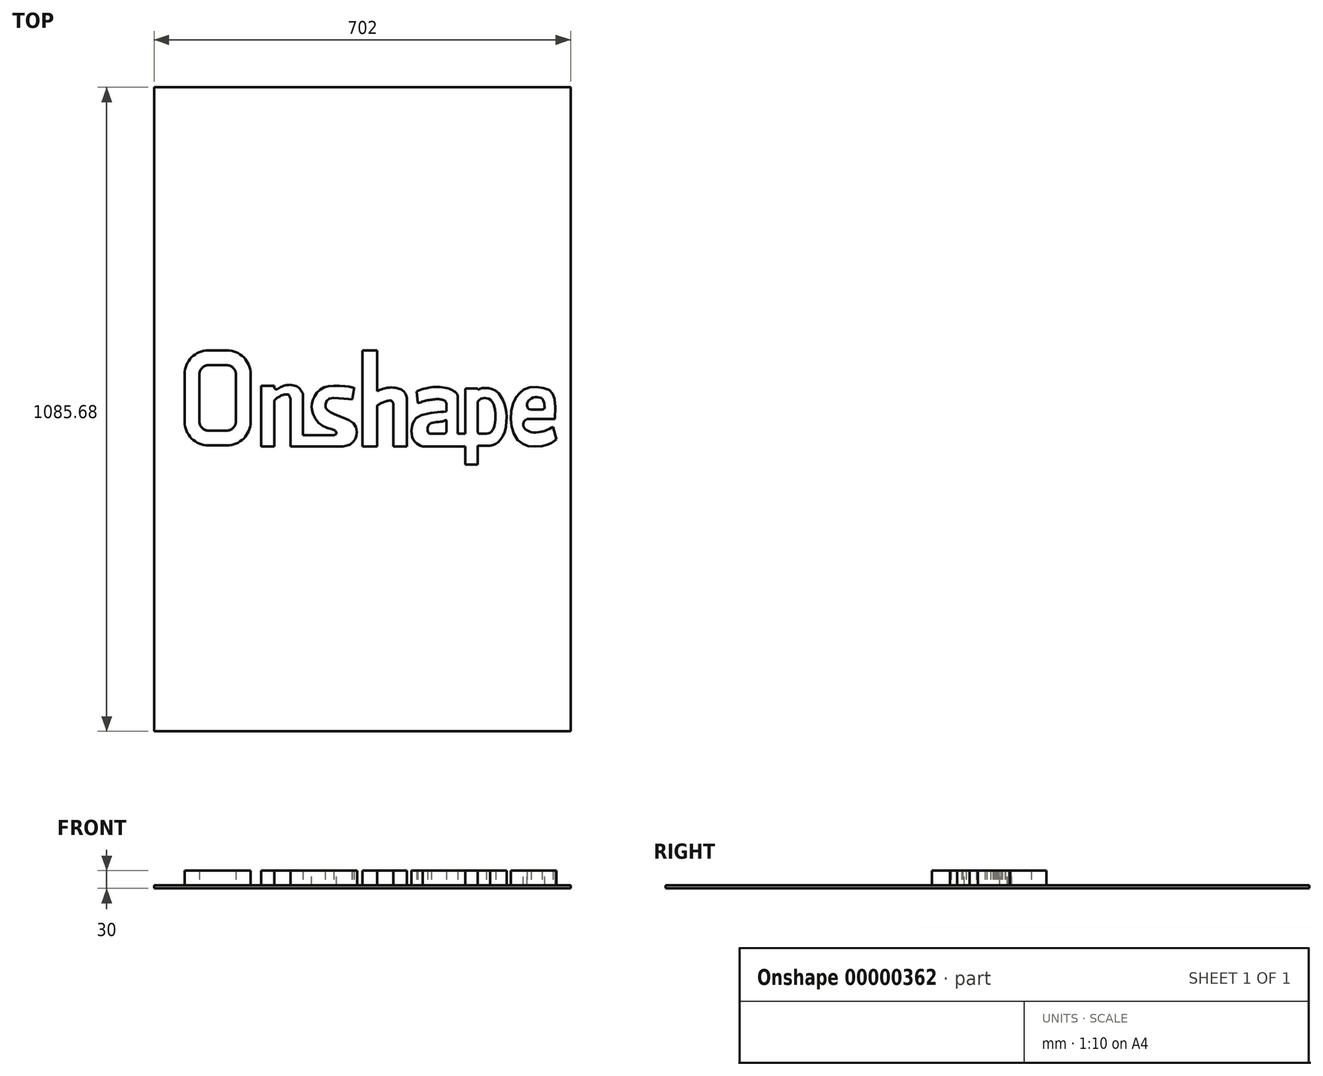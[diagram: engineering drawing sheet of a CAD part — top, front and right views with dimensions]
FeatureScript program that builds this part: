
annotation { "Feature Type Name" : "Feature", "Feature Type Description" : "" }
export const myFeature = defineFeature(function(context is Context, id is Id, definition is map)
    precondition{}
    {
        {
            var Q0;
            Q0 = qCreatedBy(makeId("Top.planeOp"), FACE);
            var sketch = newSketch(context, id + "F0", { "sketchPlane" : qUnion([Q0])});
            skLineSegment(sketch, "E0.bottom", {"start": v(-351, 542.84) * mm, "end": v(351, 542.84) * mm});
            skLineSegment(sketch, "E0.top", {"start": v(-351, -542.84) * mm, "end": v(351, -542.84) * mm});
            skLineSegment(sketch, "E0.left", {"start": v(-351, 542.84) * mm, "end": v(-351, -542.84) * mm});
            skLineSegment(sketch, "E0.right", {"start": v(351, 542.84) * mm, "end": v(351, -542.84) * mm});
            skLineSegment(sketch, "E1", {"start": v(0, 0) * mm, "end": v(285.59, 0) * mm, "construction": true});
            skLineSegment(sketch, "E2", {"start": v(0, 0) * mm, "end": v(0, 273.23) * mm, "construction": true});
            skPoint(sketch, "E3", {"position": v(351, 0) * mm});
            skPoint(sketch, "E4", {"position": v(0, 542.84) * mm});
            skSolve(sketch);
        }
        {
            var Q0;
            Q0=makeQuery(id+"F0.imprint","IMPRINT",FACE,{"disambiguationData":[TD([[makeQuery(id+"F0.imprint","IMPRINT",EDGE,{"derivedFrom":sQuery(id+"F0.wireOp",EDGE,"E0.bottom")}),-1.0]])]});
            extrude(context, id + "F1", {"entities" : qUnion([Q0]), "depth" : 5 * mm});
        }
        {
            var Q0;
            Q0=makeQuery(id+"F1.opExtrude","CAP_FACE",FACE,{"disambiguationData":[OSD([sQuery(id+"F0.wireOp",EDGE,"E0.bottom"),sQuery(id+"F0.wireOp",EDGE,"E0.top"),sQuery(id+"F0.wireOp",EDGE,"E0.left"),sQuery(id+"F0.wireOp",EDGE,"E0.right")])],"isStart":false});
            var sketch = newSketch(context, id + "F2", { "sketchPlane" : qUnion([Q0])});
            skLineSegment(sketch, "E5", {"start": v(-299.7, 59.23) * mm, "end": v(-299.7, -20.92) * mm});
            skLineSegment(sketch, "E6", {"start": v(-259.7, -60.92) * mm, "end": v(-228.47, -60.92) * mm});
            skLineSegment(sketch, "E7", {"start": v(-188.47, -20.92) * mm, "end": v(-188.47, 59.23) * mm});
            skLineSegment(sketch, "E8", {"start": v(-228.47, 99.23) * mm, "end": v(-259.7, 99.23) * mm});
            skPoint(sketch, "E9.visualSharp", {"position": v(-299.7, -60.92) * mm});
            skArc(sketch, "E9.filletArc", {"start": v(-299.7, -20.92) * mm, "mid": v(-287.98, -49.2) * mm, "end": v(-259.7, -60.92) * mm});
            skPoint(sketch, "E10.visualSharp", {"position": v(-188.47, -60.92) * mm});
            skArc(sketch, "E10.filletArc", {"start": v(-228.47, -60.92) * mm, "mid": v(-200.19, -49.2) * mm, "end": v(-188.47, -20.92) * mm});
            skPoint(sketch, "E11.visualSharp", {"position": v(-299.7, 99.23) * mm});
            skArc(sketch, "E11.filletArc", {"start": v(-259.7, 99.23) * mm, "mid": v(-287.98, 87.51) * mm, "end": v(-299.7, 59.23) * mm});
            skPoint(sketch, "E12.visualSharp", {"position": v(-188.47, 99.23) * mm});
            skArc(sketch, "E12.filletArc", {"start": v(-188.47, 59.23) * mm, "mid": v(-200.19, 87.51) * mm, "end": v(-228.47, 99.23) * mm});
            skArc(sketch, "E13.0", {"start": v(-259.7, 74.23) * mm, "mid": v(-270.3, 69.83) * mm, "end": v(-274.7, 59.23) * mm});
            skLineSegment(sketch, "E13.1", {"start": v(-228.47, 74.23) * mm, "end": v(-259.7, 74.23) * mm});
            skArc(sketch, "E13.2", {"start": v(-213.47, 59.23) * mm, "mid": v(-217.87, 69.83) * mm, "end": v(-228.47, 74.23) * mm});
            skLineSegment(sketch, "E13.3", {"start": v(-213.47, -20.92) * mm, "end": v(-213.47, 59.23) * mm});
            skArc(sketch, "E13.4", {"start": v(-228.47, -35.92) * mm, "mid": v(-217.87, -31.52) * mm, "end": v(-213.47, -20.92) * mm});
            skLineSegment(sketch, "E13.5", {"start": v(-274.7, 59.23) * mm, "end": v(-274.7, -20.92) * mm});
            skLineSegment(sketch, "E13.6", {"start": v(-259.7, -35.92) * mm, "end": v(-228.47, -35.92) * mm});
            skArc(sketch, "E13.7", {"start": v(-274.7, -20.92) * mm, "mid": v(-270.3, -31.52) * mm, "end": v(-259.7, -35.92) * mm});
            skLineSegment(sketch, "E14", {"start": v(-170.45, -62.44) * mm, "end": v(-170.45, 39.68) * mm});
            skLineSegment(sketch, "E15", {"start": v(-170.45, 39.68) * mm, "end": v(-148.72, 39.68) * mm});
            skLineSegment(sketch, "E16", {"start": v(-148.72, 39.68) * mm, "end": v(-148.72, 37.04) * mm});
            skLineSegment(sketch, "E17", {"start": v(-148.72, -62.44) * mm, "end": v(-170.45, -62.44) * mm});
            skLineSegment(sketch, "E18", {"start": v(-121.4, 17.58) * mm, "end": v(-121.4, -62.44) * mm});
            skLineSegment(sketch, "E19", {"start": v(-121.4, -62.44) * mm, "end": v(-48.13, -62.44) * mm});
            skLineSegment(sketch, "E20", {"start": v(-48.13, -43.6) * mm, "end": v(-100.29, -43.6) * mm});
            skLineSegment(sketch, "E21", {"start": v(-100.29, -43.6) * mm, "end": v(-100.29, 25.35) * mm});
            skFitSpline(sketch, "E22", {"points": [v(-148.72, 14.77) * mm, v(-138.78, 22.22) * mm, v(-125.75, 24.7) * mm, v(-121.4, 18.5) * mm], "startDerivative": vector(24.47, 22.54) * mm, "endDerivative": vector(10.61, -28.3) * mm});
            skFitSpline(sketch, "E23", {"points": [v(-148.72, 36.08) * mm, v(-146.57, 33.73) * mm, v(-143.96, 33.73) * mm, v(-137.44, 37.38) * mm, v(-127.78, 40.78) * mm, v(-114.46, 40) * mm, v(-106.37, 35.3) * mm, v(-100.29, 26.76) * mm], "startDerivative": vector(21.71, -30.96) * mm, "endDerivative": vector(33.67, -55.34) * mm});
            skLineSegment(sketch, "E24.trimOffspring", {"start": v(-148.72, 12.57) * mm, "end": v(-148.72, -62.44) * mm});
            skFitSpline(sketch, "E25", {"points": [v(-48.13, -43.6) * mm, v(-44.9, -42.6) * mm, v(-43.7, -40.64) * mm, v(-45.58, -36.09) * mm, v(-57.63, -32.04) * mm, v(-75.73, -20.85) * mm, v(-84.33, -3.82) * mm, v(-85.46, 5.7) * mm, v(-84.17, 13.46) * mm, v(-78.2, 26.16) * mm, v(-66.3, 36) * mm, v(-48.13, 39.37) * mm, v(-25.89, 38.59) * mm, v(-17.86, 37.03) * mm], "startDerivative": vector(84.75, 14.56) * mm, "endDerivative": vector(103.74, -25.5) * mm});
            skLineSegment(sketch, "E26", {"start": v(-48.13, -62.44) * mm, "end": v(-32.73, -62.44) * mm});
            skFitSpline(sketch, "E27", {"points": [v(-32.73, -62.44) * mm, v(-21.15, -59.62) * mm, v(-12.78, -51.3) * mm, v(-9.11, -40.31) * mm, v(-14.98, -23.83) * mm, v(-38.05, -12.1) * mm, v(-54.17, -4.42) * mm, v(-61.86, 2.18) * mm, v(-61.5, 11.7) * mm, v(-54.17, 18.3) * mm, v(-32.73, 17.93) * mm, v(-17.17, 16.46) * mm], "startDerivative": vector(97.21, 0) * mm, "endDerivative": vector(103.18, -17.03) * mm});
            skLineSegment(sketch, "E28", {"start": v(-17.17, 16.46) * mm, "end": v(-13.93, 36.16) * mm});
            skLineSegment(sketch, "E29", {"start": v(-13.93, 36.16) * mm, "end": v(-17.86, 37.03) * mm});
            skLineSegment(sketch, "E30", {"start": v(-0.12, -62.44) * mm, "end": v(-0.12, 99.47) * mm});
            skLineSegment(sketch, "E31", {"start": v(-0.12, 99.47) * mm, "end": v(24.62, 99.47) * mm});
            skLineSegment(sketch, "E32", {"start": v(24.62, 99.47) * mm, "end": v(24.62, 30.35) * mm});
            skLineSegment(sketch, "E33", {"start": v(24.62, -62.44) * mm, "end": v(-0.12, -62.44) * mm});
            skLineSegment(sketch, "E34", {"start": v(52.3, -62.44) * mm, "end": v(52.3, 9.6) * mm});
            skLineSegment(sketch, "E35", {"start": v(74.9, 12.38) * mm, "end": v(74.9, -62.44) * mm});
            skLineSegment(sketch, "E36", {"start": v(74.9, -62.44) * mm, "end": v(52.3, -62.44) * mm});
            skFitSpline(sketch, "E37", {"points": [v(24.62, 5.44) * mm, v(27.86, 8.13) * mm, v(34.95, 11.8) * mm, v(43.26, 14.24) * mm, v(49.13, 14) * mm, v(51.82, 10.75) * mm, v(52.3, 8.38) * mm], "startDerivative": vector(19.33, 17.96) * mm, "endDerivative": vector(0, -32.88) * mm});
            skFitSpline(sketch, "E38", {"points": [v(24.62, 30.35) * mm, v(29.1, 32.6) * mm, v(36.01, 34.84) * mm, v(42.58, 36.4) * mm, v(53.13, 36.4) * mm, v(62.46, 34.5) * mm, v(70.24, 29.66) * mm, v(74.22, 22.05) * mm, v(74.9, 15.3) * mm, v(74.9, 12.38) * mm], "startDerivative": vector(44.62, 25.05) * mm, "endDerivative": vector(-0.44, -37.07) * mm});
            skLineSegment(sketch, "E39.trimOffspring", {"start": v(24.62, 5.44) * mm, "end": v(24.62, -62.44) * mm});
            skFitSpline(sketch, "E40", {"points": [v(91.47, 29.81) * mm, v(100.87, 33.76) * mm, v(109.8, 36) * mm, v(121.47, 37.76) * mm, v(137.6, 36.75) * mm, v(148.95, 33.38) * mm, v(156.51, 28.8) * mm, v(160.7, 22.33) * mm], "startDerivative": vector(46.04, 27.08) * mm, "endDerivative": vector(2.85, -63.73) * mm});
            skLineSegment(sketch, "E41", {"start": v(160.7, 22.33) * mm, "end": v(160.7, -41.26) * mm});
            skLineSegment(sketch, "E42", {"start": v(101.8, -62.44) * mm, "end": v(173.45, -62.44) * mm});
            skFitSpline(sketch, "E43", {"points": [v(101.8, -62.44) * mm, v(94.97, -60.1) * mm, v(89.25, -55.3) * mm, v(84.04, -47.25) * mm, v(82.98, -33.71) * mm, v(84.45, -25.96) * mm, v(89.86, -15.84) * mm, v(100.35, -9.98) * mm, v(114.96, -6.23) * mm, v(130.08, -4.58) * mm, v(141.68, -3.82) * mm], "startDerivative": vector(-83.06, 22.5) * mm, "endDerivative": vector(90.2, 15.78) * mm});
            skLineSegment(sketch, "E44", {"start": v(141.68, -3.82) * mm, "end": v(141.68, 9.14) * mm});
            skLineSegment(sketch, "E45", {"start": v(91.47, 29.81) * mm, "end": v(93.14, 10.22) * mm});
            skFitSpline(sketch, "E46", {"points": [v(93.14, 10.22) * mm, v(102.54, 13.17) * mm, v(110.48, 15.2) * mm, v(119.18, 16.47) * mm, v(126.74, 17.06) * mm, v(133.29, 16.56) * mm, v(138.37, 14.63) * mm, v(141.68, 9.14) * mm], "startDerivative": vector(58.12, 18.51) * mm, "endDerivative": vector(-2.77, -59.3) * mm});
            skLineSegment(sketch, "E47", {"start": v(141.68, -18.9) * mm, "end": v(141.68, -36.46) * mm});
            skLineSegment(sketch, "E48", {"start": v(116.36, -41.46) * mm, "end": v(136.68, -41.46) * mm});
            skFitSpline(sketch, "E49", {"points": [v(116.36, -41.46) * mm, v(112.4, -40.43) * mm, v(110.68, -38.46) * mm, v(109.69, -34.27) * mm, v(110.68, -28.76) * mm, v(114.38, -24.32) * mm, v(123.1, -21.93) * mm, v(132.88, -20.86) * mm, v(136.9, -19.71) * mm, v(139.17, -18.9) * mm, v(140.44, -18.15) * mm, v(141.3, -18.44) * mm, v(141.68, -18.9) * mm], "startDerivative": vector(-49.56, 8.3) * mm, "endDerivative": vector(5.14, -15.4) * mm});
            skLineSegment(sketch, "E50", {"start": v(160.7, -41.26) * mm, "end": v(173.45, -41.26) * mm});
            skLineSegment(sketch, "E51", {"start": v(173.45, -41.26) * mm, "end": v(173.45, 33.12) * mm});
            skLineSegment(sketch, "E52", {"start": v(173.45, -62.44) * mm, "end": v(173.45, -93.45) * mm});
            skLineSegment(sketch, "E53", {"start": v(173.45, -93.45) * mm, "end": v(194.65, -93.45) * mm});
            skLineSegment(sketch, "E54", {"start": v(194.65, -93.45) * mm, "end": v(194.65, -61.56) * mm});
            skLineSegment(sketch, "E55", {"start": v(194.65, -61.56) * mm, "end": v(215.6, -61.56) * mm});
            skLineSegment(sketch, "E56", {"start": v(194.65, -38.26) * mm, "end": v(194.65, 12.53) * mm});
            skLineSegment(sketch, "E57", {"start": v(175.45, 35.12) * mm, "end": v(194.65, 35.12) * mm});
            skLineSegment(sketch, "E58", {"start": v(197.65, -41.26) * mm, "end": v(209.14, -41.26) * mm});
            skFitSpline(sketch, "E59", {"points": [v(194.65, 12.53) * mm, v(197.22, 15.65) * mm, v(199.78, 17.28) * mm, v(203.26, 18.68) * mm, v(208.38, 18.9) * mm, v(214.66, 16.82) * mm, v(220.24, 10.54) * mm, v(224.2, -3.65) * mm, v(224.2, -18.53) * mm, v(222.34, -29.23) * mm, v(217.92, -37.6) * mm, v(213.5, -40.4) * mm, v(209.14, -41.26) * mm], "startDerivative": vector(39.46, 54.88) * mm, "endDerivative": vector(-66.44, -9.1) * mm});
            skFitSpline(sketch, "E60", {"points": [v(194.65, 35.12) * mm, v(194.65, 34.24) * mm, v(195.2, 33.45) * mm, v(197.3, 33.82) * mm, v(200.08, 35.12) * mm, v(204.76, 35.8) * mm, v(215.73, 35.12) * mm, v(226.27, 30.15) * mm, v(232.85, 22.81) * mm, v(239.05, 10.48) * mm, v(242.37, -1.64) * mm, v(243.18, -18.11) * mm, v(240.18, -36.82) * mm, v(233.54, -50.2) * mm, v(226.74, -57.3) * mm, v(221.64, -59.78) * mm, v(215.6, -61.56) * mm], "startDerivative": vector(-4.32, -40.56) * mm, "endDerivative": vector(-113.2, -25.5) * mm});
            skPoint(sketch, "E61.orphan", {"position": v(160.7, 22.88) * mm});
            skFitSpline(sketch, "E62", {"points": [v(326.96, -50.83) * mm, v(320.02, -56.08) * mm, v(315.24, -58.6) * mm, v(309.1, -60.81) * mm, v(299.72, -62.54) * mm, v(285.17, -62.73) * mm, v(276.37, -60.93) * mm, v(268.48, -56.75) * mm, v(259.32, -48.7) * mm, v(253.39, -35.65) * mm, v(250.61, -20.8) * mm, v(250.93, -3.85) * mm, v(254.2, 10.02) * mm, v(259.94, 21.4) * mm, v(265.37, 27.44) * mm, v(270.42, 32.05) * mm, v(278.77, 36) * mm, v(290.84, 37.54) * mm, v(303.57, 36.22) * mm, v(313.45, 33.15) * mm, v(318.72, 29.2) * mm, v(322.67, 21.95) * mm, v(324.64, 13.83) * mm, v(324.86, -16.25) * mm], "startDerivative": vector(-94.33, -93.91) * mm, "endDerivative": vector(-10.07, -512.06) * mm});
            skLineSegment(sketch, "E63", {"start": v(324.86, -16.25) * mm, "end": v(277.89, -16.25) * mm});
            skFitSpline(sketch, "E64", {"points": [v(277.89, -16.25) * mm, v(273.27, -19.98) * mm, v(271.31, -24.74) * mm, v(271.72, -28.5) * mm, v(273.39, -32) * mm, v(276.36, -34.76) * mm, v(281.36, -37.5) * mm, v(290.54, -39.2) * mm, v(302.45, -37.83) * mm, v(308.36, -35.97) * mm, v(315.28, -32.97) * mm, v(321.28, -29.83) * mm], "startDerivative": vector(-38.92, -19.1) * mm, "endDerivative": vector(57.68, 31.07) * mm});
            skLineSegment(sketch, "E65", {"start": v(321.28, -29.83) * mm, "end": v(326.96, -50.83) * mm});
            skLineSegment(sketch, "E66", {"start": v(284.38, -0.68) * mm, "end": v(303.3, -0.68) * mm});
            skFitSpline(sketch, "E67", {"points": [v(303.3, -0.68) * mm, v(305.2, -0.1) * mm, v(306.86, 1.74) * mm, v(307.15, 5.36) * mm, v(306.8, 10.1) * mm, v(304.71, 15.56) * mm, v(301.1, 19.05) * mm, v(295.06, 20.33) * mm, v(287.73, 19.63) * mm, v(282.73, 16.6) * mm, v(279.6, 13.57) * mm, v(277.7, 8.85) * mm, v(278.01, 3.51) * mm, v(280.22, 0.9) * mm, v(284.38, -0.68) * mm], "startDerivative": vector(39.67, 11.95) * mm, "endDerivative": vector(102.32, -7.72) * mm});
            skArc(sketch, "E68.filletArc", {"start": v(194.65, -38.26) * mm, "mid": v(195.53, -40.38) * mm, "end": v(197.65, -41.26) * mm});
            skLineSegment(sketch, "E69.extension", {"start": v(-148.12, 35.24) * mm, "end": v(-148.12, 35.24) * mm});
            skArc(sketch, "E70.filletArc", {"start": v(-148.72, 37.04) * mm, "mid": v(-148.57, 36.1) * mm, "end": v(-148.12, 35.24) * mm});
            skArc(sketch, "E71.filletArc", {"start": v(136.68, -41.46) * mm, "mid": v(140.22, -40) * mm, "end": v(141.68, -36.46) * mm});
            skLineSegment(sketch, "E72.extension", {"start": v(-147.06, 16.28) * mm, "end": v(-147.06, 16.28) * mm});
            skArc(sketch, "E73.filletArc", {"start": v(-147.06, 16.28) * mm, "mid": v(-148.29, 14.6) * mm, "end": v(-148.72, 12.57) * mm});
            skArc(sketch, "E74.filletArc", {"start": v(-100.29, 25.35) * mm, "mid": v(-100.48, 26.71) * mm, "end": v(-101.03, 27.97) * mm});
            skArc(sketch, "E75.filletArc", {"start": v(-121.4, 17.58) * mm, "mid": v(-121.48, 18.5) * mm, "end": v(-121.73, 19.38) * mm});
            skArc(sketch, "E76.filletArc", {"start": v(175.45, 35.12) * mm, "mid": v(174.04, 34.54) * mm, "end": v(173.45, 33.12) * mm});
            skSolve(sketch);
        }
        {
            var Q0;
            {Q0=qUnion([makeQuery(id+"F2.imprint","IMPRINT",FACE,{"disambiguationData":[TD([[makeQuery(id+"F2.imprint","IMPRINT",EDGE,{"derivedFrom":sQuery(id+"F2.wireOp",EDGE,"E14")}),-1.0]])]}),makeQuery(id+"F2.imprint","IMPRINT",FACE,{"disambiguationData":[TD([[makeQuery(id+"F2.imprint","IMPRINT",EDGE,{"derivedFrom":sQuery(id+"F2.wireOp",EDGE,"E30")}),-1.0]])]}),makeQuery(id+"F2.imprint","IMPRINT",FACE,{"disambiguationData":[TD([[makeQuery(id+"F2.imprint","IMPRINT",EDGE,{"derivedFrom":sQuery(id+"F2.wireOp",EDGE,"E5")}),1.0]])]}),makeQuery(id+"F2.imprint","IMPRINT",FACE,{"disambiguationData":[TD([[makeQuery(id+"F2.imprint","IMPRINT",EDGE,{"derivedFrom":sQuery(id+"F2.wireOp",EDGE,"E62")}),-1.0]])]}),makeQuery(id+"F2.imprint","IMPRINT",FACE,{"disambiguationData":[TD([[makeQuery(id+"F2.imprint","IMPRINT",EDGE,{"derivedFrom":sQuery(id+"F2.wireOp",EDGE,"E40")}),-1.0]])]})]);}
            extrude(context, id + "F3", {"entities" : qUnion([Q0]), "operationType" : NewBodyOperationType.ADD, "depth" : 25 * mm});
        }
    });
